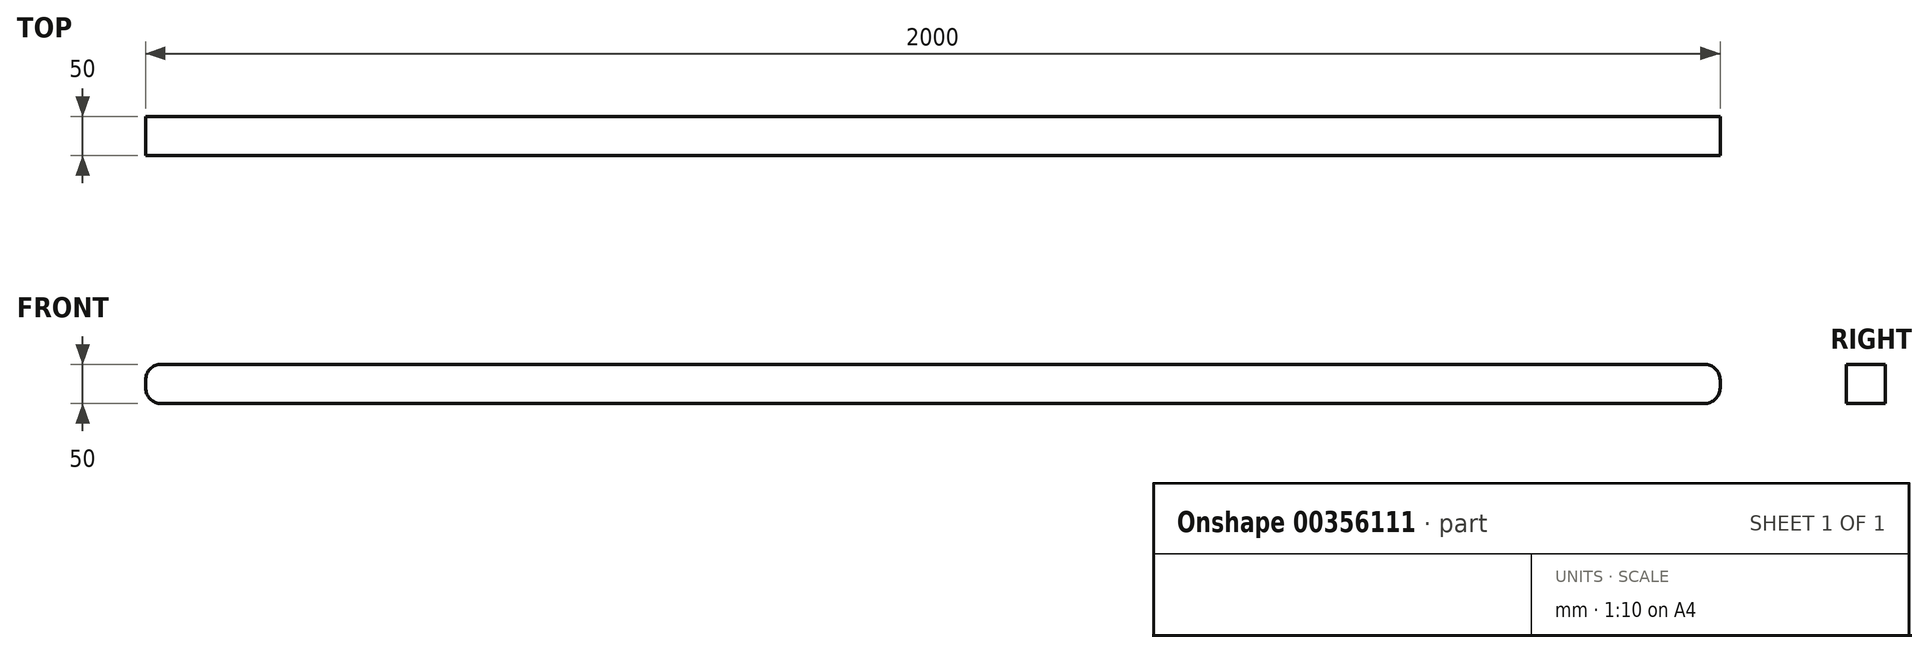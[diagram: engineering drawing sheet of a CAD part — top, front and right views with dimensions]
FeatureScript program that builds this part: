
annotation { "Feature Type Name" : "Feature", "Feature Type Description" : "" }
export const myFeature = defineFeature(function(context is Context, id is Id, definition is map)
    precondition{}
    {
        {
            var Q0;
            Q0=qCreatedBy(makeId("Front.planeOp"),FACE);
            var sketch = newSketch(context, id + "F0", { "sketchPlane" : qUnion([Q0])});
            skLineSegment(sketch, "E0.bottom", {"start": v(-175.15, 17.14) * mm, "end": v(1824.85, 17.14) * mm});
            skLineSegment(sketch, "E0.top", {"start": v(-175.15, -32.86) * mm, "end": v(1824.85, -32.86) * mm});
            skLineSegment(sketch, "E0.left", {"start": v(-175.15, 17.14) * mm, "end": v(-175.15, -32.86) * mm});
            skLineSegment(sketch, "E0.right", {"start": v(1824.85, 17.14) * mm, "end": v(1824.85, -32.86) * mm});
            skSolve(sketch);
        }
        {
            var Q0;
            Q0=makeQuery(id+"F0.imprint","IMPRINT",FACE,{"disambiguationData":[TD([[makeQuery(id+"F0.imprint","IMPRINT",EDGE,{"derivedFrom":sQuery(id+"F0.wireOp",EDGE,"E0.bottom")}),-1.0]])]});
            extrude(context, id + "F1", {"entities" : qUnion([Q0]), "endBound" : BoundingType.SYMMETRIC, "depth" : 50 * mm});
        }
        {
            var Q0;
            Q0=makeQuery(id+"F1.opExtrude","SWEPT_EDGE",EDGE,{"disambiguationData":[OSD([sQuery(id+"F0.wireOp",EDGE,"E0.bottom"),sQuery(id+"F0.wireOp",EDGE,"E0.right")])]});
            var Q1;
            Q1=makeQuery(id+"F1.opExtrude","SWEPT_EDGE",EDGE,{"disambiguationData":[OSD([sQuery(id+"F0.wireOp",EDGE,"E0.top"),sQuery(id+"F0.wireOp",EDGE,"E0.right")])]});
            var Q2;
            Q2=makeQuery(id+"F1.opExtrude","SWEPT_EDGE",EDGE,{"disambiguationData":[OSD([sQuery(id+"F0.wireOp",EDGE,"E0.bottom"),sQuery(id+"F0.wireOp",EDGE,"E0.left")])]});
            var Q3;
            Q3=makeQuery(id+"F1.opExtrude","SWEPT_EDGE",EDGE,{"disambiguationData":[OSD([sQuery(id+"F0.wireOp",EDGE,"E0.top"),sQuery(id+"F0.wireOp",EDGE,"E0.left")])]});
            fillet(context, id + "F2", {"entities" : qUnion([Q0, Q1, Q2, Q3]), "radius" : 20 * mm, "tangentPropagation" : true, "allowEdgeOverflow" : false});
        }
    });
